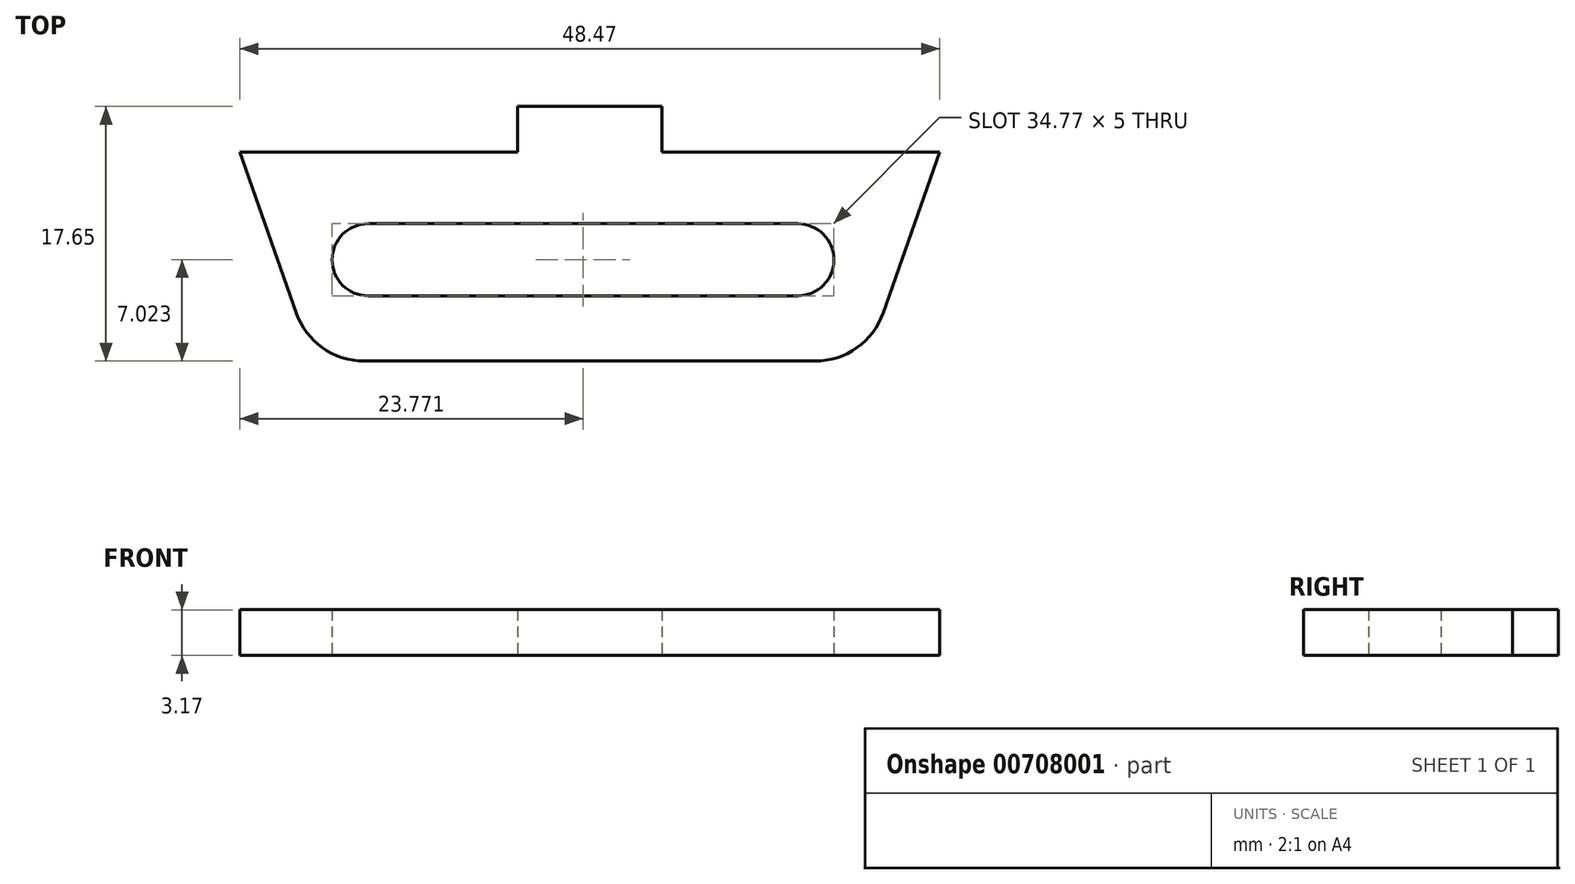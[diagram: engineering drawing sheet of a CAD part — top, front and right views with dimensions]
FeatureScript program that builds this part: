
annotation { "Feature Type Name" : "Feature", "Feature Type Description" : "" }
export const myFeature = defineFeature(function(context is Context, id is Id, definition is map)
    precondition{}
    {
        {
            var Q0;
            Q0=qCreatedBy(makeId("Top.planeOp"), FACE);
            var sketch = newSketch(context, id + "F0", { "sketchPlane" : qUnion([Q0])});
            skPoint(sketch, "E0.0", {"position": v(-28.2, 49.2) * mm});
            skPoint(sketch, "E1.0", {"position": v(20.26, 49.2) * mm});
            skLineSegment(sketch, "E2.0", {"start": v(1.02, 1.85) * mm, "end": v(20.26, 1.85) * mm});
            skLineSegment(sketch, "E3.0", {"start": v(-28.2, 1.85) * mm, "end": v(-8.98, 1.85) * mm});
            skLineSegment(sketch, "E4", {"start": v(20.26, 49.2) * mm, "end": v(20.26, 1.85) * mm, "construction": true});
            skLineSegment(sketch, "E5", {"start": v(-28.2, 49.2) * mm, "end": v(-28.2, 1.85) * mm, "construction": true});
            skPoint(sketch, "E6.orphan", {"position": v(28.9, 1.85) * mm});
            skLineSegment(sketch, "E7", {"start": v(20.26, 1.85) * mm, "end": v(16.36, -9.28) * mm});
            skLineSegment(sketch, "E8.0", {"start": v(1.02, 5.02) * mm, "end": v(1.02, 1.85) * mm});
            skLineSegment(sketch, "E9.0", {"start": v(-3.98, 5.02) * mm, "end": v(1.02, 5.02) * mm});
            skLineSegment(sketch, "E10.0", {"start": v(-3.98, 5.02) * mm, "end": v(-8.98, 5.02) * mm});
            skLineSegment(sketch, "E11.0", {"start": v(-8.98, 5.02) * mm, "end": v(-8.98, 1.85) * mm});
            skLineSegment(sketch, "E12.MirrorCS", {"start": v(-28.2, 1.85) * mm, "end": v(-24.31, -9.28) * mm});
            skLineSegment(sketch, "E13", {"start": v(11.64, -12.63) * mm, "end": v(-19.6, -12.63) * mm});
            skLineSegment(sketch, "E14", {"start": v(-3.98, 5.02) * mm, "end": v(-3.98, -12.63) * mm, "construction": true});
            skArc(sketch, "E15.0.startCap", {"start": v(10.44, -3.1) * mm, "mid": v(12.94, -5.6) * mm, "end": v(10.44, -8.1) * mm});
            skArc(sketch, "E15.0.endCap", {"start": v(-19.32, -8.1) * mm, "mid": v(-21.82, -5.6) * mm, "end": v(-19.32, -3.1) * mm});
            skLineSegment(sketch, "E15.0.left", {"start": v(10.44, -8.1) * mm, "end": v(-19.32, -8.1) * mm});
            skLineSegment(sketch, "E15.0.right", {"start": v(10.44, -3.1) * mm, "end": v(-19.32, -3.1) * mm});
            skPoint(sketch, "E16.visualSharp", {"position": v(15.19, -12.63) * mm});
            skArc(sketch, "E16.filletArc", {"start": v(11.64, -12.63) * mm, "mid": v(14.53, -11.7) * mm, "end": v(16.36, -9.28) * mm});
            skPoint(sketch, "E17.visualSharp", {"position": v(-23.14, -12.63) * mm});
            skArc(sketch, "E17.filletArc", {"start": v(-24.31, -9.28) * mm, "mid": v(-22.48, -11.7) * mm, "end": v(-19.6, -12.63) * mm});
            skPoint(sketch, "E18.orphan", {"position": v(-36.85, 1.85) * mm});
            skPoint(sketch, "E19.0.end.orphan", {"position": v(17.9, -12.63) * mm});
            skPoint(sketch, "E19.0.start.orphan", {"position": v(22.97, 1.85) * mm});
            skSolve(sketch);
        }
        {
            var Q0;
            Q0 = qSketchRegion(id + "F0", true);
            extrude(context, id + "F1", {"entities" : qUnion([Q0]), "depth" : 3.17 * mm, "offsetDistance" : 25 * mm});
        }
    });
